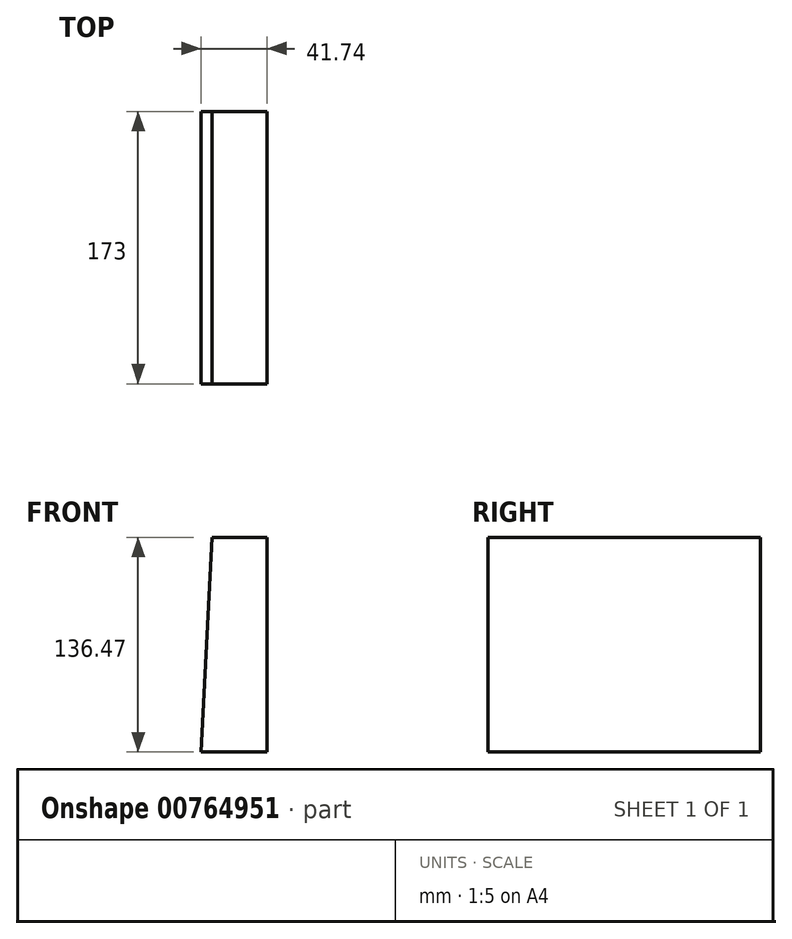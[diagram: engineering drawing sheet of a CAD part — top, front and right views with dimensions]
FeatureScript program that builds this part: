
annotation { "Feature Type Name" : "Feature", "Feature Type Description" : "" }
export const myFeature = defineFeature(function(context is Context, id is Id, definition is map)
    precondition{}
    {
        {
            var Q0;
            Q0=qCreatedBy(makeId("Front.planeOp"),FACE);
            var sketch = newSketch(context, id + "F0", { "sketchPlane" : qUnion([Q0])});
            skLineSegment(sketch, "E0", {"start": v(0, 0) * mm, "end": v(41.74, 0) * mm});
            skLineSegment(sketch, "E1", {"start": v(41.74, 0) * mm, "end": v(41.74, 136.47) * mm});
            skLineSegment(sketch, "E2", {"start": v(41.74, 136.47) * mm, "end": v(6.78, 136.47) * mm});
            skLineSegment(sketch, "E3", {"start": v(6.78, 136.47) * mm, "end": v(0, 0) * mm});
            skSolve(sketch);
        }
        {
            var Q0;
            Q0=makeQuery(id+"F0.imprint","IMPRINT",FACE,{"disambiguationData":[TD([[makeQuery(id+"F0.imprint","IMPRINT",EDGE,{"derivedFrom":sQuery(id+"F0.wireOp",EDGE,"E0")}),1.0]])]});
            extrude(context, id + "F1", {"entities" : qUnion([Q0]), "depth" : 173 * mm, "offsetDistance" : 25 * mm});
        }
    });
